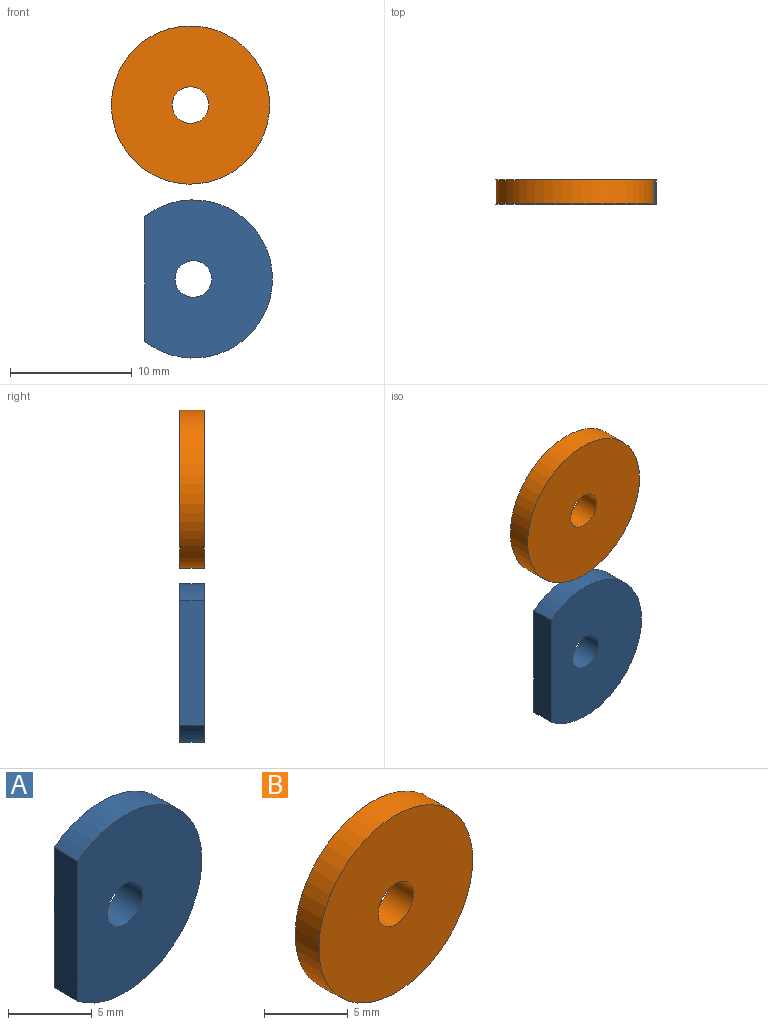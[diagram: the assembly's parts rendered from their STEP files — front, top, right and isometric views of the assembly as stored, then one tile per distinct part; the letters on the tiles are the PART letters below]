
ASSEMBLY  parts=2 mates=1
PART A: 5 faces, bbox 10.5x2x13 mm
  f0: cylinder r=6.5mm len=13mm, axis (0,1,0), area 58.1mm2, adj f2,f3,f4
  f1: cylinder r=1.5mm len=3mm, axis (0,1,0), area 18.8mm2, adj f3,f4
  f2: plane 10.25x2mm, normal (-1,0,0), area 20.5mm2, adj f0,f3,f4
  f3: plane 13x10.5mm, normal (0,-1,0), area 107.8mm2, adj f0,f1,f2
  f4: plane 13x10.5mm, normal (0,1,0), area 107.8mm2, adj f0,f1,f2
PART B: 4 faces, bbox 13x2x13 mm
  f0: cylinder r=1.5mm len=3mm, axis (0,1,0), area 18.8mm2, adj f2,f3
  f1: cylinder r=6.5mm len=13mm, axis (0,1,0), area 81.7mm2, adj f2,f3
  f2: plane 13x13mm, normal (0,-1,0), area 125.7mm2, adj f0,f1
  f3: plane 13x13mm, normal (0,1,0), area 125.7mm2, adj f0,f1
PLACE A t=(-2.61,-0.16,-5.62)mm
PLACE B t=(-2.84,-0.16,-6.32)mm
MATE planar A.f3 <-> B.f0  axis (0,-1,0) through (-47.75,-2.16,26.24)mm
